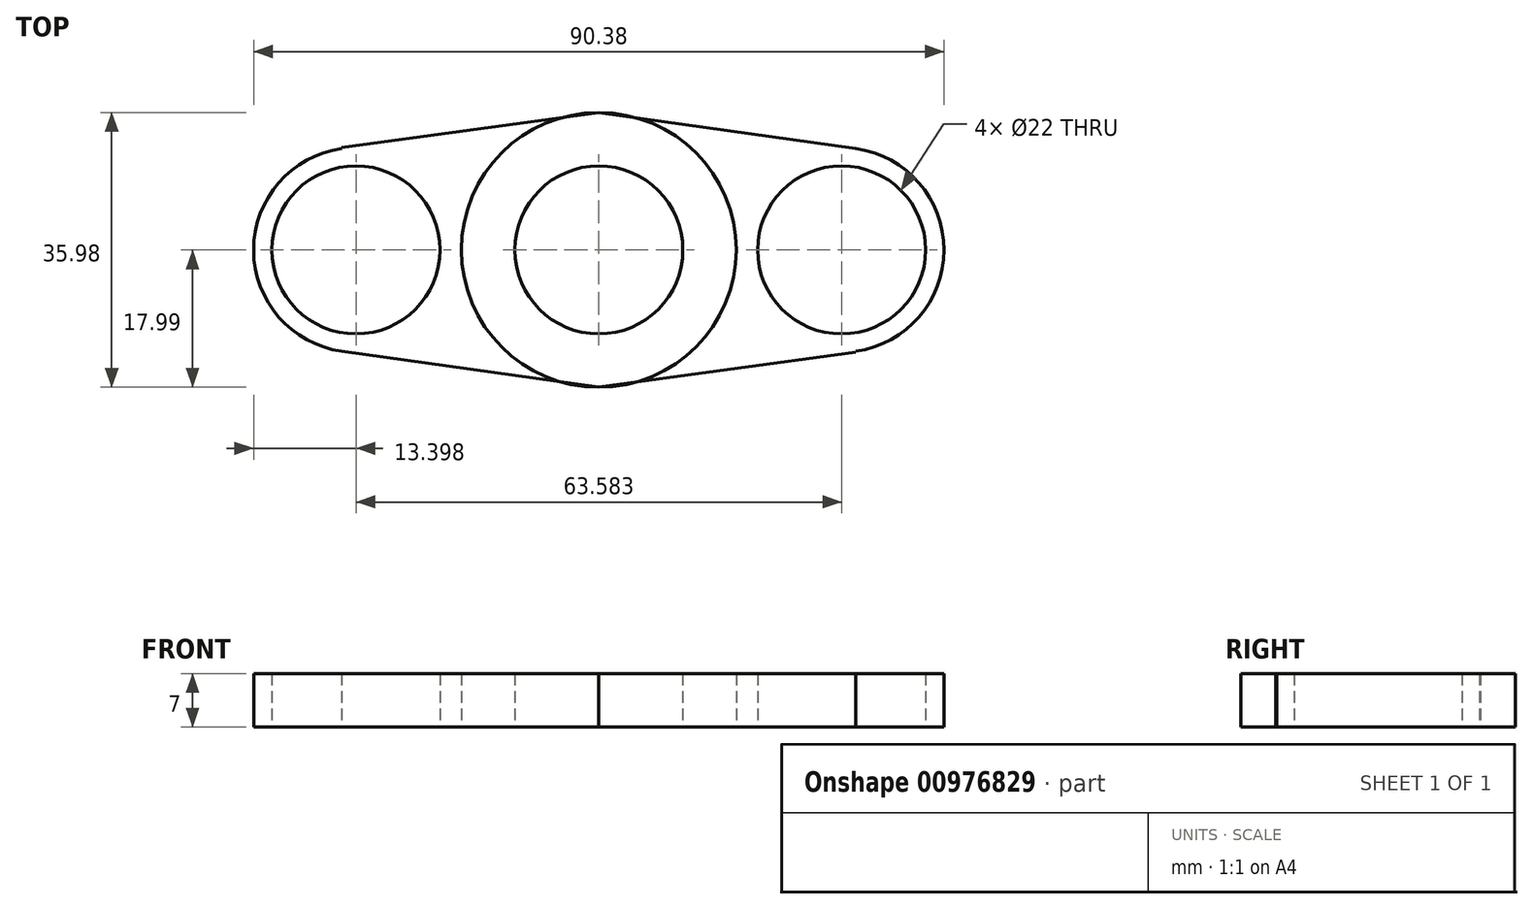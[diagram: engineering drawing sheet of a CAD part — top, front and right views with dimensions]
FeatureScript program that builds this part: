
annotation { "Feature Type Name" : "Feature", "Feature Type Description" : "" }
export const myFeature = defineFeature(function(context is Context, id is Id, definition is map)
    precondition{}
    {
        {
            var Q0;
            Q0=qCreatedBy(makeId("Top.planeOp"),FACE);
            var sketch = newSketch(context, id + "F0", { "sketchPlane" : qUnion([Q0])});
            skCircle(sketch, "E0", {"center": v(0, 0) * mm, "radius": 11 * mm});
            skCircle(sketch, "E1", {"center": v(0, 0) * mm, "radius": 18 * mm});
            skLineSegment(sketch, "E2", {"start": v(0, 18) * mm, "end": v(33.65, 13.27) * mm});
            skLineSegment(sketch, "E3", {"start": v(0, -18) * mm, "end": v(33.65, -13.4) * mm});
            skLineSegment(sketch, "E4", {"start": v(33.65, -13.4) * mm, "end": v(33.65, -13.27) * mm});
            skArc(sketch, "E5", {"start": v(33.65, -13.27) * mm, "mid": v(45.2, 0) * mm, "end": v(33.65, 13.27) * mm});
            skCircle(sketch, "E6", {"center": v(31.8, 0) * mm, "radius": 11 * mm});
            skSolve(sketch);
        }
        {
            var Q0;
            {var subQ0=sQuery(id+"F0.wireOp",EDGE,"ScoDwn3W-GFTI-MH0O-xd9y-ZgtUPaaMcwjz");var subQ1=sQuery(id+"F0.wireOp",EDGE,"E1");var subQ2=makeQuery(id+"F0.imprint","INTERSECT",VERTEX,{"derivedFrom":[subQ1,subQ0]});Q0=makeQuery(id+"F0.imprint","IMPRINT",FACE,{"disambiguationData":[TD([[makeQuery(id+"F0.imprint","IMPRINT",EDGE,{"disambiguationData":[TD([[subQ2,-1.0]])],"derivedFrom":subQ1}),-1.0]])]});}
            var Q1;
            Q1=makeQuery(id+"F0.imprint","IMPRINT",FACE,{"disambiguationData":[TD([[makeQuery(id+"F0.imprint","IMPRINT",EDGE,{"derivedFrom":sQuery(id+"F0.wireOp",EDGE,"E0")}),-1.0]])]});
            var Q2;
            {var subQ0=sQuery(id+"F0.wireOp",EDGE,"fdHwjECG-iqMA-TczR-qPu5-q6pd7nmDPv54");Q2=makeQuery(id+"F0.imprint","IMPRINT",FACE,{"disambiguationData":[TD([[makeQuery(id+"F0.imprint","IMPRINT",EDGE,{"derivedFrom":subQ0}),-1.0]])]});}
            var Q3;
            {var subQ0=sQuery(id+"F0.wireOp",EDGE,"fdHwjECG-iqMA-TczR-qPu5-q6pd7nmDPv54");Q3=makeQuery(id+"F0.imprint","IMPRINT",FACE,{"disambiguationData":[TD([[makeQuery(id+"F0.imprint","IMPRINT",EDGE,{"derivedFrom":subQ0}),1.0]])]});}
            var Q4;
            {var subQ0=sQuery(id+"F0.wireOp",EDGE,"E4");var subQ1=sQuery(id+"F0.wireOp",EDGE,"ecpM7z9a-sqwW-KDQ1-7jH7-bRJ6ZcL4zhRn");var subQ3=makeQuery(id+"F0.imprint","INTERSECT",VERTEX,{"derivedFrom":[subQ1,subQ0]});Q4=makeQuery(id+"F0.imprint","IMPRINT",FACE,{"disambiguationData":[TD([[makeQuery(id+"F0.imprint","IMPRINT",EDGE,{"disambiguationData":[TD([[subQ3,1.0]])],"derivedFrom":subQ1}),1.0]])]});}
            var Q5;
            {var subQ0=sQuery(id+"F0.wireOp",EDGE,"E4");var subQ1=sQuery(id+"F0.wireOp",EDGE,"ecpM7z9a-sqwW-KDQ1-7jH7-bRJ6ZcL4zhRn");var subQ3=makeQuery(id+"F0.imprint","INTERSECT",VERTEX,{"derivedFrom":[subQ1,subQ0]});Q5=makeQuery(id+"F0.imprint","IMPRINT",FACE,{"disambiguationData":[TD([[makeQuery(id+"F0.imprint","IMPRINT",EDGE,{"disambiguationData":[TD([[subQ3,-1.0]])],"derivedFrom":subQ1}),1.0]])]});}
            extrude(context, id + "F1", {"entities" : qUnion([Q0, Q1, Q2, Q3, Q4, Q5]), "depth" : 7 * mm, "offsetDistance" : 25 * mm, "symmetric" : true});
        }
        {
            var Q0;
            Q0=makeQuery(id+"F1.opExtrude","SWEPT_BODY",BODY,{"disambiguationData":[OSD([sQuery(id+"F0.wireOp",EDGE,"E0"),sQuery(id+"F0.wireOp",EDGE,"E1"),sQuery(id+"F0.wireOp",EDGE,"ecpM7z9a-sqwW-KDQ1-7jH7-bRJ6ZcL4zhRn"),sQuery(id+"F0.wireOp",EDGE,"E2"),sQuery(id+"F0.wireOp",EDGE,"E3"),sQuery(id+"F0.wireOp",EDGE,"E4")])]});
            var Q1;
            Q1=makeQuery(id+"F1.opExtrude","CAP_EDGE",EDGE,{"disambiguationData":[OSD([sQuery(id+"F0.wireOp",EDGE,"E1")])],"isStart":false});
            circularPattern(context, id + "F2", {"entities" : qUnion([Q0]), "axis" : qUnion([Q1]), "angle" : 360 * degree, "instanceCount" : 2, "equalSpace" : true});
        }
    });
